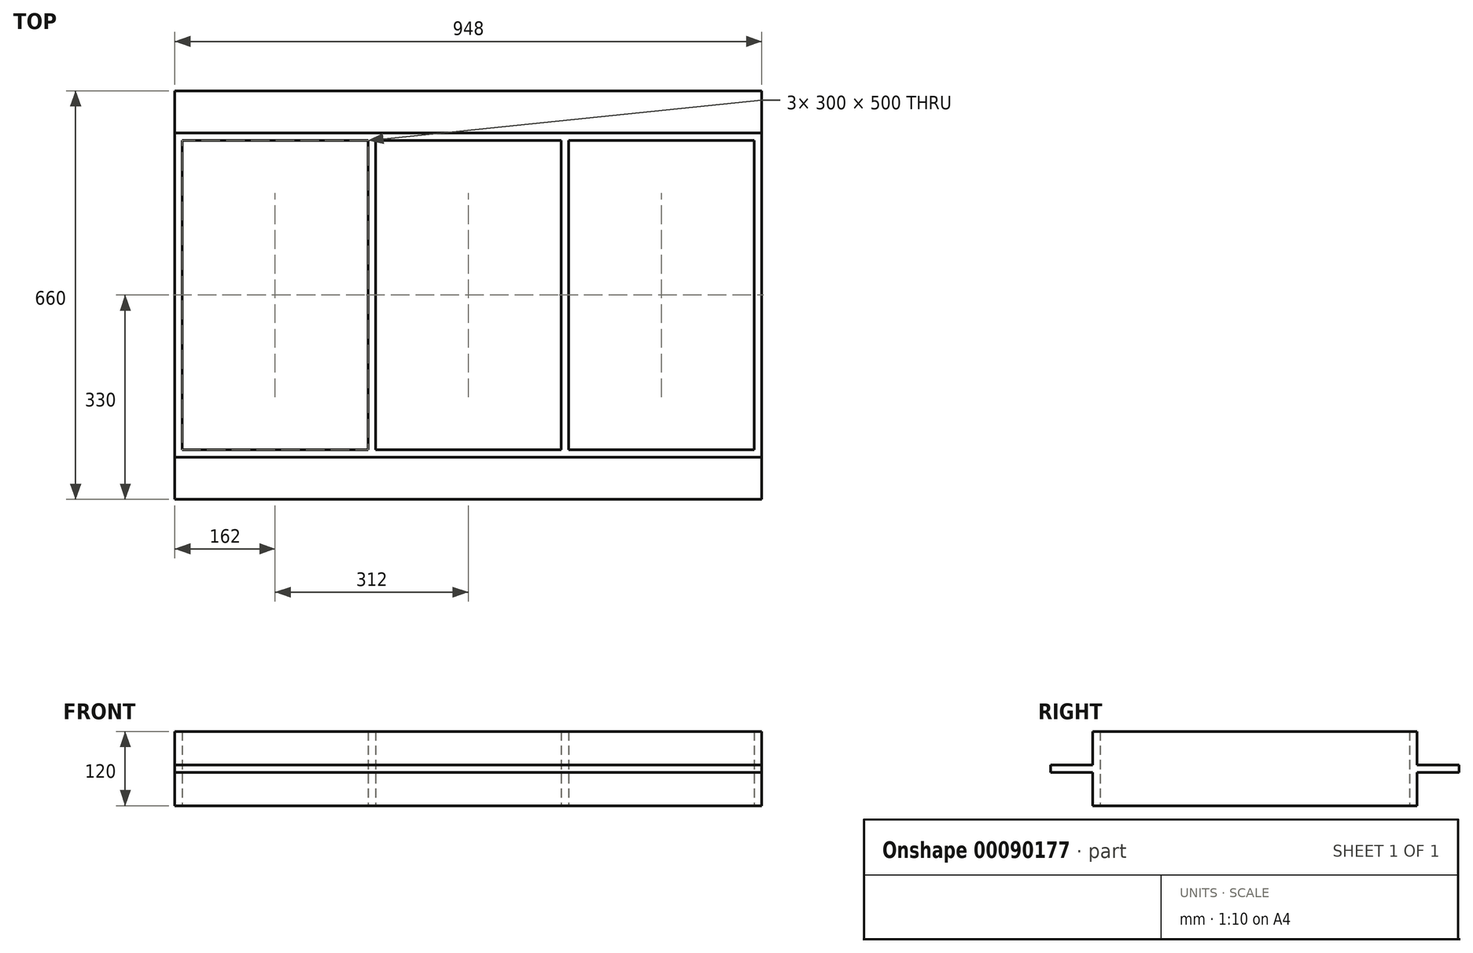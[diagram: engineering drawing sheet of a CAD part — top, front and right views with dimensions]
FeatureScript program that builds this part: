
annotation { "Feature Type Name" : "Feature", "Feature Type Description" : "" }
export const myFeature = defineFeature(function(context is Context, id is Id, definition is map)
    precondition{}
    {
        {
            var Q0;
            Q0=qCreatedBy(makeId("Top.planeOp"),FACE);
            var sketch = newSketch(context, id + "F0", { "sketchPlane" : qUnion([Q0])});
            skLineSegment(sketch, "E0.bottom", {"start": v(-150, -250) * mm, "end": v(150, -250) * mm});
            skLineSegment(sketch, "E0.top", {"start": v(-150, 250) * mm, "end": v(150, 250) * mm});
            skLineSegment(sketch, "E0.left", {"start": v(-150, -250) * mm, "end": v(-150, 250) * mm});
            skLineSegment(sketch, "E0.right", {"start": v(150, -250) * mm, "end": v(150, 250) * mm});
            skPoint(sketch, "E0.middle", {"position": v(0, 0) * mm});
            skLineSegment(sketch, "E1.0", {"start": v(-474, 262) * mm, "end": v(474, 262) * mm});
            skLineSegment(sketch, "E1.2", {"start": v(-474, -262) * mm, "end": v(474, -262) * mm});
            skLineSegment(sketch, "E2.bottom", {"start": v(162, 250) * mm, "end": v(462, 250) * mm});
            skLineSegment(sketch, "E2.top", {"start": v(162, -250) * mm, "end": v(462, -250) * mm});
            skLineSegment(sketch, "E2.left", {"start": v(162, 250) * mm, "end": v(162, -250) * mm});
            skLineSegment(sketch, "E2.right", {"start": v(462, 250) * mm, "end": v(462, -250) * mm});
            skLineSegment(sketch, "E3.bottom", {"start": v(-162, 250) * mm, "end": v(-462, 250) * mm});
            skLineSegment(sketch, "E3.top", {"start": v(-162, -250) * mm, "end": v(-462, -250) * mm});
            skLineSegment(sketch, "E3.left", {"start": v(-162, 250) * mm, "end": v(-162, -250) * mm});
            skLineSegment(sketch, "E3.right", {"start": v(-462, 250) * mm, "end": v(-462, -250) * mm});
            skLineSegment(sketch, "E4.0", {"start": v(-474, 262) * mm, "end": v(-474, -262) * mm});
            skLineSegment(sketch, "E5.0", {"start": v(474, 262) * mm, "end": v(474, -262) * mm});
            skSolve(sketch);
        }
        {
            var Q0;
            Q0=makeQuery(id+"F0.imprint","IMPRINT",FACE,{"disambiguationData":[TD([[makeQuery(id+"F0.imprint","IMPRINT",EDGE,{"derivedFrom":sQuery(id+"F0.wireOp",EDGE,"E0.bottom")}),-1.0]])]});
            extrude(context, id + "F1", {"entities" : qUnion([Q0]), "depth" : 120 * mm});
        }
        {
            var Q0;
            Q0=makeQuery(id+"F1.opExtrude","SWEPT_FACE",FACE,{"disambiguationData":[OSD([sQuery(id+"F0.wireOp",EDGE,"E4.0")])]});
            var sketch = newSketch(context, id + "F2", { "sketchPlane" : qUnion([Q0])});
            skLineSegment(sketch, "E6", {"start": v(-420.92, 60) * mm, "end": v(384.5, 60) * mm, "construction": true});
            skPoint(sketch, "E6.startSnap0", {"position": v(-262, 60) * mm});
            skLineSegment(sketch, "E7", {"start": v(-262, 54) * mm, "end": v(-330, 54) * mm});
            skLineSegment(sketch, "E8", {"start": v(-330, 54) * mm, "end": v(-330, 60) * mm});
            skLineSegment(sketch, "E9", {"start": v(0, 0) * mm, "end": v(0, 120) * mm, "construction": true});
            skLineSegment(sketch, "E10.MirrorCS", {"start": v(-330, 66) * mm, "end": v(-330, 60) * mm});
            skLineSegment(sketch, "E11.MirrorCS", {"start": v(-262, 66) * mm, "end": v(-330, 66) * mm});
            skLineSegment(sketch, "E12.MirrorCS", {"start": v(330, 54) * mm, "end": v(330, 60) * mm});
            skLineSegment(sketch, "E13.MirrorCS", {"start": v(330, 66) * mm, "end": v(330, 60) * mm});
            skLineSegment(sketch, "E14.MirrorCS", {"start": v(262, 66) * mm, "end": v(330, 66) * mm});
            skLineSegment(sketch, "E15.MirrorCS", {"start": v(262, 54) * mm, "end": v(330, 54) * mm});
            skSolve(sketch);
        }
        {
            var Q0;
            {var subQ1=sQuery(id+"F2.wireOp",EDGE,"E7");Q0=makeQuery(id+"F2.imprint","IMPRINT",FACE,{"disambiguationData":[TD([[makeQuery(id+"F2.imprint","IMPRINT",EDGE,{"derivedFrom":subQ1}),-1.0]])]});}
            var Q1;
            Q1=makeQuery(id+"F2.imprint","IMPRINT",FACE,{"disambiguationData":[TD([[makeQuery(id+"F2.imprint","IMPRINT",EDGE,{"derivedFrom":sQuery(id+"F2.wireOp",EDGE,"E12.MirrorCS")}),1.0]])]});
            var Q2;
            Q2=makeQuery(id+"F1.opExtrude","SWEPT_FACE",FACE,{"disambiguationData":[OSD([sQuery(id+"F0.wireOp",EDGE,"E5.0")])]});
            extrude(context, id + "F3", {"entities" : qUnion([Q0, Q1]), "operationType" : NewBodyOperationType.ADD, "endBound" : BoundingType.UP_TO_SURFACE, "oppositeDirection" : true, "endBoundEntityFace" : qUnion([Q2]), "depth" : 25 * mm});
        }
    });
